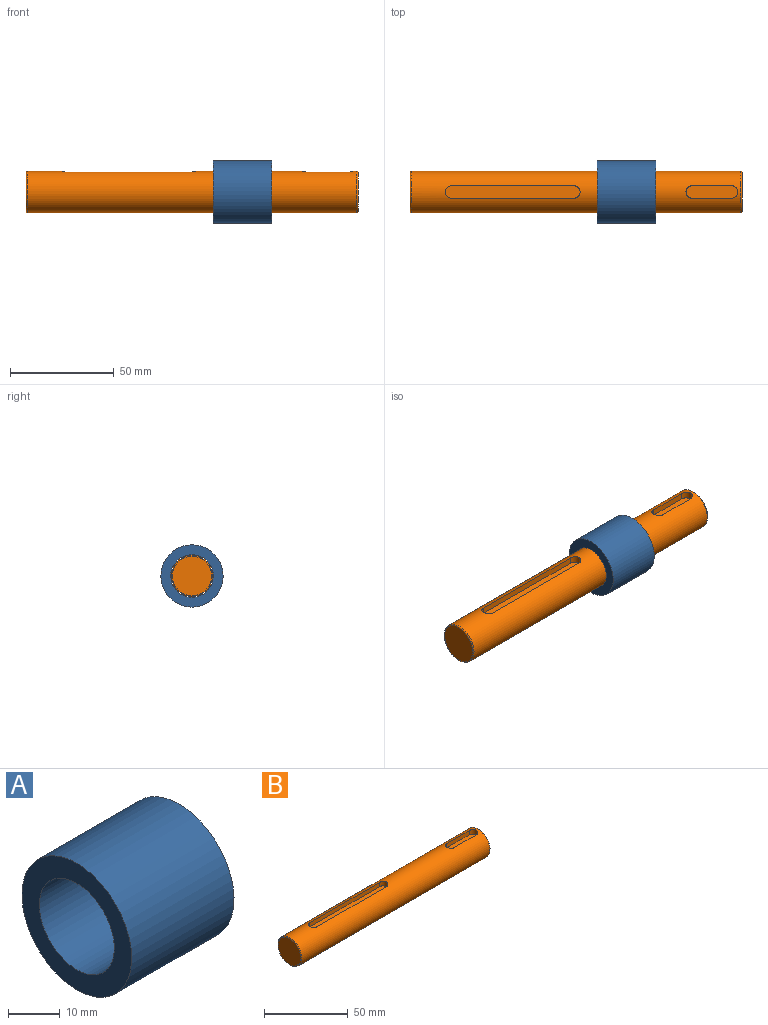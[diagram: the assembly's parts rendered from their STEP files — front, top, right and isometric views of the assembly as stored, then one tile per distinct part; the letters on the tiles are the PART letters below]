
ASSEMBLY  parts=2 mates=1
PART A: 4 faces, bbox 28x30x30 mm
  f0: cylinder r=10.25mm len=28mm, axis (-1,0,0), area 1803.3mm2, adj f2,f3
  f1: cylinder r=15mm len=30mm, axis (-1,0,0), area 2638.9mm2, adj f2,f3
  f2: plane 30x30mm, normal (1,0,0), area 376.8mm2, adj f0,f1
  f3: plane 30x30mm, normal (-1,0,0), area 376.8mm2, adj f0,f1
PART B: 15 faces, bbox 160x21.6x21.6 mm
  f0: cylinder r=10mm len=159mm, axis (-1,0,0), area 9457.7mm2, adj f3,f4,f5,f6,f7,f8,f10,f11
  f1: plane 19x19mm, normal (1,0,0), area 283.5mm2, adj f4
  f2: plane 19x19mm, normal (-1,0,0), area 283.5mm2, adj f3
  f3: torus R=9.5mm, axis (1,0,0), area 48.5mm2, adj f0,f2
  f4: torus R=9.5mm, axis (1,0,0), area 48.5mm2, adj f0,f1
  f5: plane 19x3.04mm, normal (0,-1,0), area 57.7mm2, adj f0,f6,f8,f9
  f6: cylinder r=3mm len=6mm, axis (0,0,1), area 30.8mm2, adj f0,f5,f7,f9
  f7: plane 19x3.04mm, normal (0,1,0), area 57.7mm2, adj f0,f6,f8,f9
  f8: cylinder r=3mm len=6mm, axis (0,0,1), area 30.8mm2, adj f0,f5,f7,f9
  f9: plane 25x6mm, normal (0,0,1), area 142.3mm2, adj f5,f6,f7,f8
  f10: plane 59x3.04mm, normal (0,-1,0), area 179.3mm2, adj f0,f11,f13,f14
  f11: cylinder r=3mm len=6mm, axis (0,0,1), area 30.8mm2, adj f0,f10,f12,f14
  f12: plane 59x3.04mm, normal (0,1,0), area 179.3mm2, adj f0,f11,f13,f14
  f13: cylinder r=3mm len=6mm, axis (0,0,1), area 30.8mm2, adj f0,f10,f12,f14
  f14: plane 65x6mm, normal (0,0,1), area 382.3mm2, adj f10,f11,f12,f13
PLACE A t=(-2.2,185.46,21.86)mm
PLACE B t=(-26.55,-14.54,21.86)mm
MATE slider A.f0 <-> B.f0  axis (-1,0,0) through (11.8,-14.54,21.86)mm
